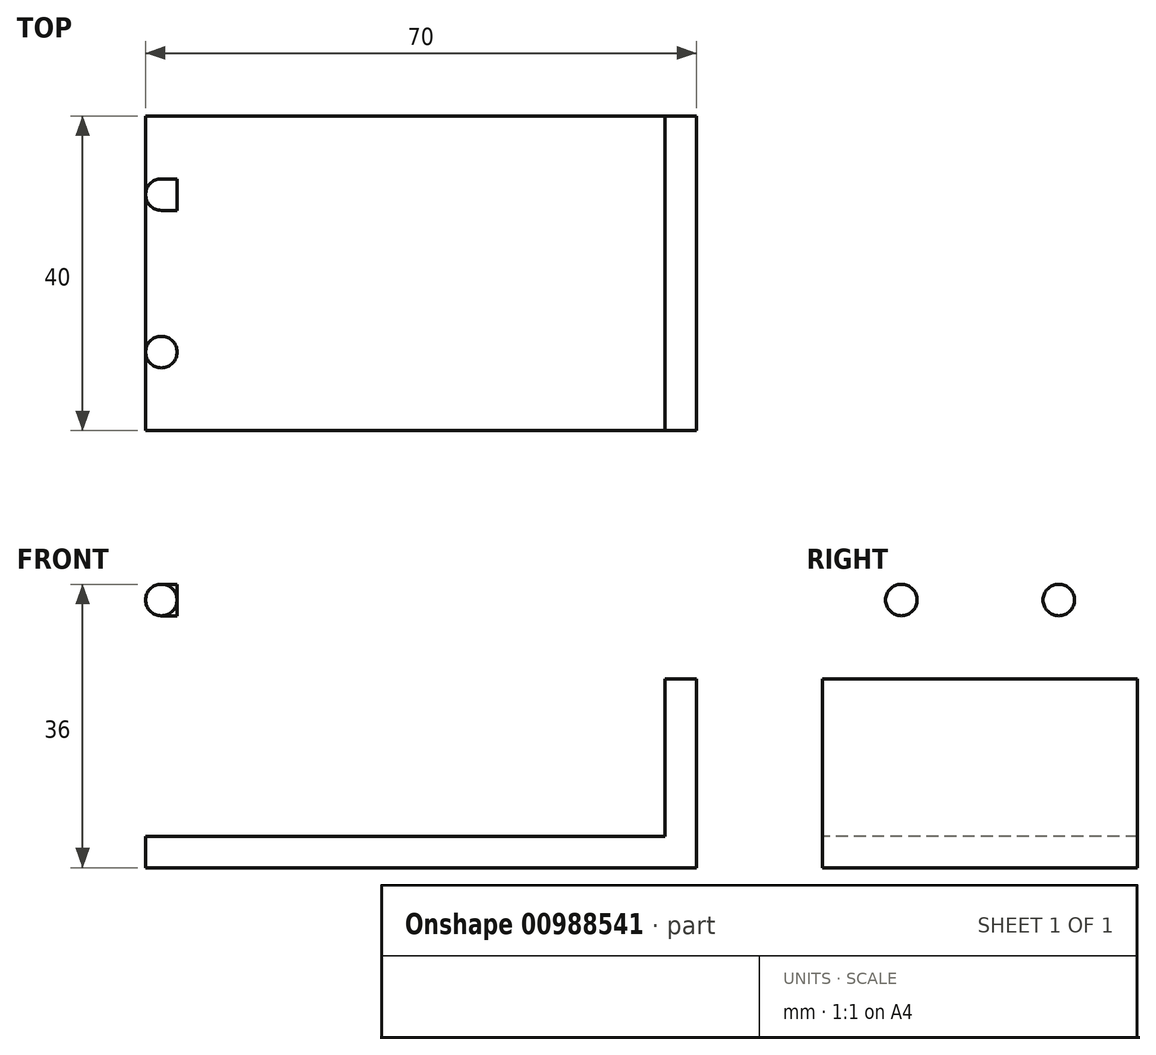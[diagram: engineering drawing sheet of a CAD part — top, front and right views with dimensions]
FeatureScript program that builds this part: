
annotation { "Feature Type Name" : "Feature", "Feature Type Description" : "" }
export const myFeature = defineFeature(function(context is Context, id is Id, definition is map)
    precondition{}
    {
        {
            var Q0;
            Q0=qCreatedBy(makeId("Top.planeOp"),FACE);
            var sketch = newSketch(context, id + "F0", { "sketchPlane" : qUnion([Q0])});
            skLineSegment(sketch, "E0.bottom", {"start": v(-33, 20) * mm, "end": v(33, 20) * mm});
            skLineSegment(sketch, "E0.top", {"start": v(-33, -20) * mm, "end": v(33, -20) * mm});
            skLineSegment(sketch, "E0.left", {"start": v(-33, 20) * mm, "end": v(-33, -20) * mm});
            skLineSegment(sketch, "E0.right", {"start": v(33, 20) * mm, "end": v(33, -20) * mm});
            skPoint(sketch, "E0.middle", {"position": v(0, 0) * mm});
            skSolve(sketch);
        }
        {
            var Q0;
            Q0=makeQuery(id+"F0.imprint","IMPRINT",FACE,{"disambiguationData":[TD([[makeQuery(id+"F0.imprint","IMPRINT",EDGE,{"derivedFrom":sQuery(id+"F0.wireOp",EDGE,"E0.bottom")}),-1.0]])]});
            extrude(context, id + "F1", {"entities" : qUnion([Q0]), "depth" : 2 * mm, "offsetDistance" : 25 * mm});
        }
        {
            var Q0;
            Q0=makeQuery(id+"F1.opExtrude","CAP_FACE",FACE,{"disambiguationData":[OSD([sQuery(id+"F0.wireOp",EDGE,"E0.bottom"),sQuery(id+"F0.wireOp",EDGE,"E0.top"),sQuery(id+"F0.wireOp",EDGE,"E0.left"),sQuery(id+"F0.wireOp",EDGE,"E0.right")])],"isStart":false});
            var sketch = newSketch(context, id + "F2", { "sketchPlane" : qUnion([Q0])});
            skLineSegment(sketch, "E1", {"start": v(-31, 20) * mm, "end": v(-31, -20) * mm});
            skLineSegment(sketch, "E2", {"start": v(31, 20) * mm, "end": v(31, -20) * mm});
            skSolve(sketch);
        }
        {
            var Q0;
            {var subQ0=sQuery(id+"F2.wireOp",EDGE,"E1");Q0=makeQuery(id+"F2.imprint","IMPRINT",FACE,{"disambiguationData":[TD([[makeQuery(id+"F2.imprint","IMPRINT",EDGE,{"derivedFrom":subQ0}),-1.0]])]});}
            var Q1;
            {var subQ0=sQuery(id+"F2.wireOp",EDGE,"E2");Q1=makeQuery(id+"F2.imprint","IMPRINT",FACE,{"disambiguationData":[TD([[makeQuery(id+"F2.imprint","IMPRINT",EDGE,{"derivedFrom":subQ0}),1.0]])]});}
            extrude(context, id + "F3", {"entities" : qUnion([Q0, Q1]), "operationType" : NewBodyOperationType.ADD, "depth" : 20 * mm, "offsetDistance" : 25 * mm});
        }
        {
            var Q0;
            Q0=makeQuery(id+"F3.opExtrude","CAP_FACE",FACE,{"disambiguationData":[OSD([sQuery(id+"F0.wireOp",EDGE,"E0.bottom"),sQuery(id+"F0.wireOp",EDGE,"E0.top"),sQuery(id+"F0.wireOp",EDGE,"E0.left"),sQuery(id+"F2.wireOp",EDGE,"E1")])],"isStart":false});
            extrude(context, id + "F4", {"entities" : qUnion([Q0]), "operationType" : NewBodyOperationType.ADD, "depth" : 20 * mm, "offsetDistance" : 25 * mm});
        }
        {
            var Q0;
            {var subQ0=sQuery(id+"F0.wireOp",EDGE,"E0.left");Q0=makeQuery(id+"F4.boolean.opBoolean","MERGE",FACE,{"derivedFrom":[makeQuery(id+"F3.boolean.opBoolean","MERGE",FACE,{"derivedFrom":[makeQuery(id+"F1.opExtrude","SWEPT_FACE",FACE,{"disambiguationData":[OSD([subQ0])]}),makeQuery(id+"F3.opExtrude","SWEPT_FACE",FACE,{"disambiguationData":[OSD([subQ0])]})]}),makeQuery(id+"F4.opExtrude","SWEPT_FACE",FACE,{"disambiguationData":[OSD([subQ0])]})]});}
            extrude(context, id + "F5", {"entities" : qUnion([Q0]), "operationType" : NewBodyOperationType.ADD, "depth" : 2 * mm, "offsetDistance" : 25 * mm});
        }
        {
            var Q0;
            {var subQ0=sQuery(id+"F0.wireOp",EDGE,"E0.right");Q0=makeQuery(id+"F3.boolean.opBoolean","MERGE",FACE,{"derivedFrom":[makeQuery(id+"F1.opExtrude","SWEPT_FACE",FACE,{"disambiguationData":[OSD([subQ0])]}),makeQuery(id+"F3.opExtrude","SWEPT_FACE",FACE,{"disambiguationData":[OSD([subQ0])]})]});}
            extrude(context, id + "F6", {"entities" : qUnion([Q0]), "operationType" : NewBodyOperationType.ADD, "depth" : 2 * mm, "offsetDistance" : 25 * mm});
        }
        {
            var Q0;
            {var subQ0=sQuery(id+"F0.wireOp",EDGE,"E0.right");var subQ1=sQuery(id+"F0.wireOp",EDGE,"E0.left");Q0=makeQuery(id+"F6.boolean.opBoolean","MERGE",FACE,{"derivedFrom":[makeQuery(id+"F5.boolean.opBoolean","MERGE",FACE,{"derivedFrom":[makeQuery(id+"F1.opExtrude","CAP_FACE",FACE,{"disambiguationData":[OSD([sQuery(id+"F0.wireOp",EDGE,"E0.bottom"),sQuery(id+"F0.wireOp",EDGE,"E0.top"),subQ1,subQ0])],"isStart":true}),makeQuery(id+"F5.opExtrude","SWEPT_FACE",FACE,{"disambiguationData":[OSD([subQ1]),TDD([makeQuery(id+"F1.opExtrude","CAP_EDGE",EDGE,{"disambiguationData":[OSD([subQ1])],"isStart":true})])]})]}),makeQuery(id+"F6.opExtrude","SWEPT_FACE",FACE,{"disambiguationData":[OSD([subQ0]),TDD([makeQuery(id+"F1.opExtrude","CAP_EDGE",EDGE,{"disambiguationData":[OSD([subQ0])],"isStart":true})])]})]});}
            extrude(context, id + "F7", {"entities" : qUnion([Q0]), "operationType" : NewBodyOperationType.ADD, "depth" : 2 * mm, "offsetDistance" : 25 * mm});
        }
        {
            var Q0;
            {var subQ0=sQuery(id+"F2.wireOp",EDGE,"E1");Q0=makeQuery(id+"F4.boolean.opBoolean","MERGE",FACE,{"derivedFrom":[makeQuery(id+"F3.opExtrude","SWEPT_FACE",FACE,{"disambiguationData":[OSD([subQ0])]}),makeQuery(id+"F4.opExtrude","SWEPT_FACE",FACE,{"disambiguationData":[OSD([subQ0])]})]});}
            var sketch = newSketch(context, id + "F8", { "sketchPlane" : qUnion([Q0])});
            skLineSegment(sketch, "E3", {"start": v(-10, 42) * mm, "end": v(-10, 2) * mm});
            skLineSegment(sketch, "E4", {"start": v(10, 42) * mm, "end": v(10, 2) * mm});
            skPoint(sketch, "E5", {"position": v(-10, 32) * mm});
            skPoint(sketch, "E6", {"position": v(10, 32) * mm});
            skCircle(sketch, "E7", {"center": v(-10, 32) * mm, "radius": 2 * mm});
            skCircle(sketch, "E8", {"center": v(10, 32) * mm, "radius": 2 * mm});
            skSolve(sketch);
        }
        {
            var Q0;
            {var subQ0=sQuery(id+"F8.wireOp",EDGE,"E7");var subQ1=sQuery(id+"F8.wireOp",EDGE,"E3");var subQ2=makeQuery(id+"F8.imprint","INTERSECT",VERTEX,{"disambiguationData":[OD(0.0)],"derivedFrom":[subQ1,subQ0]});Q0=makeQuery(id+"F8.imprint","IMPRINT",FACE,{"disambiguationData":[TD([[makeQuery(id+"F8.imprint","IMPRINT",EDGE,{"disambiguationData":[TD([[subQ2,-1.0]])],"derivedFrom":subQ1}),-1.0]])]});}
            var Q1;
            {var subQ0=sQuery(id+"F8.wireOp",EDGE,"E7");var subQ1=sQuery(id+"F8.wireOp",EDGE,"E3");var subQ2=makeQuery(id+"F8.imprint","INTERSECT",VERTEX,{"disambiguationData":[OD(0.0)],"derivedFrom":[subQ1,subQ0]});Q1=makeQuery(id+"F8.imprint","IMPRINT",FACE,{"disambiguationData":[TD([[makeQuery(id+"F8.imprint","IMPRINT",EDGE,{"disambiguationData":[TD([[subQ2,-1.0]])],"derivedFrom":subQ1}),1.0]])]});}
            var Q2;
            {var subQ0=sQuery(id+"F8.wireOp",EDGE,"E8");var subQ1=sQuery(id+"F8.wireOp",EDGE,"E4");var subQ2=makeQuery(id+"F8.imprint","INTERSECT",VERTEX,{"disambiguationData":[OD(0.0)],"derivedFrom":[subQ1,subQ0]});Q2=makeQuery(id+"F8.imprint","IMPRINT",FACE,{"disambiguationData":[TD([[makeQuery(id+"F8.imprint","IMPRINT",EDGE,{"disambiguationData":[TD([[subQ2,-1.0]])],"derivedFrom":subQ1}),-1.0]])]});}
            var Q3;
            {var subQ0=sQuery(id+"F8.wireOp",EDGE,"E8");var subQ1=sQuery(id+"F8.wireOp",EDGE,"E4");var subQ2=makeQuery(id+"F8.imprint","INTERSECT",VERTEX,{"disambiguationData":[OD(0.0)],"derivedFrom":[subQ1,subQ0]});Q3=makeQuery(id+"F8.imprint","IMPRINT",FACE,{"disambiguationData":[TD([[makeQuery(id+"F8.imprint","IMPRINT",EDGE,{"disambiguationData":[TD([[subQ2,-1.0]])],"derivedFrom":subQ1}),1.0]])]});}
            extrude(context, id + "F9", {"entities" : qUnion([Q0, Q1, Q2, Q3]), "operationType" : NewBodyOperationType.REMOVE, "oppositeDirection" : true, "depth" : 25 * mm, "offsetDistance" : 25 * mm});
        }
        {
            var Q0;
            Q0=makeQuery(id+"F9.boolean.opBoolean","COPY",EDGE,{"derivedFrom":makeQuery(id+"F9.opExtrude","CAP_EDGE",EDGE,{"disambiguationData":[OSD([sQuery(id+"F8.wireOp",EDGE,"E7")])],"isStart":true})});
            var Q1;
            Q1=makeQuery(id+"F9.boolean.opBoolean","COPY",EDGE,{"derivedFrom":makeQuery(id+"F9.opExtrude","CAP_EDGE",EDGE,{"disambiguationData":[OSD([sQuery(id+"F8.wireOp",EDGE,"E8")])],"isStart":true})});
            fillet(context, id + "F10", {"entities" : qUnion([Q0, Q1]), "radius" : 2 * mm, "tangentPropagation" : true, "allowEdgeOverflow" : false});
        }
        {
            var Q0;
            {var subQ0=sQuery(id+"F0.wireOp",EDGE,"E0.left");Q0=makeQuery(id+"F9.boolean.opBoolean","INTERSECT",EDGE,{"derivedFrom":[makeQuery(id+"F7.boolean.opBoolean","MERGE",FACE,{"derivedFrom":[makeQuery(id+"F5.opExtrude","CAP_FACE",FACE,{"disambiguationData":[OSD([subQ0])],"isStart":false}),makeQuery(id+"F7.opExtrude","SWEPT_FACE",FACE,{"disambiguationData":[OSD([subQ0])]})]}),makeQuery(id+"F9.opExtrude","SWEPT_FACE",FACE,{"disambiguationData":[OSD([sQuery(id+"F8.wireOp",EDGE,"E8")])]})]});}
            var Q1;
            {var subQ0=sQuery(id+"F0.wireOp",EDGE,"E0.left");Q1=makeQuery(id+"F9.boolean.opBoolean","INTERSECT",EDGE,{"derivedFrom":[makeQuery(id+"F7.boolean.opBoolean","MERGE",FACE,{"derivedFrom":[makeQuery(id+"F5.opExtrude","CAP_FACE",FACE,{"disambiguationData":[OSD([subQ0])],"isStart":false}),makeQuery(id+"F7.opExtrude","SWEPT_FACE",FACE,{"disambiguationData":[OSD([subQ0])]})]}),makeQuery(id+"F9.opExtrude","SWEPT_FACE",FACE,{"disambiguationData":[OSD([sQuery(id+"F8.wireOp",EDGE,"E7")])]})]});}
            fillet(context, id + "F11", {"entities" : qUnion([Q0, Q1]), "radius" : 2 * mm, "tangentPropagation" : true, "allowEdgeOverflow" : false});
        }
    });
